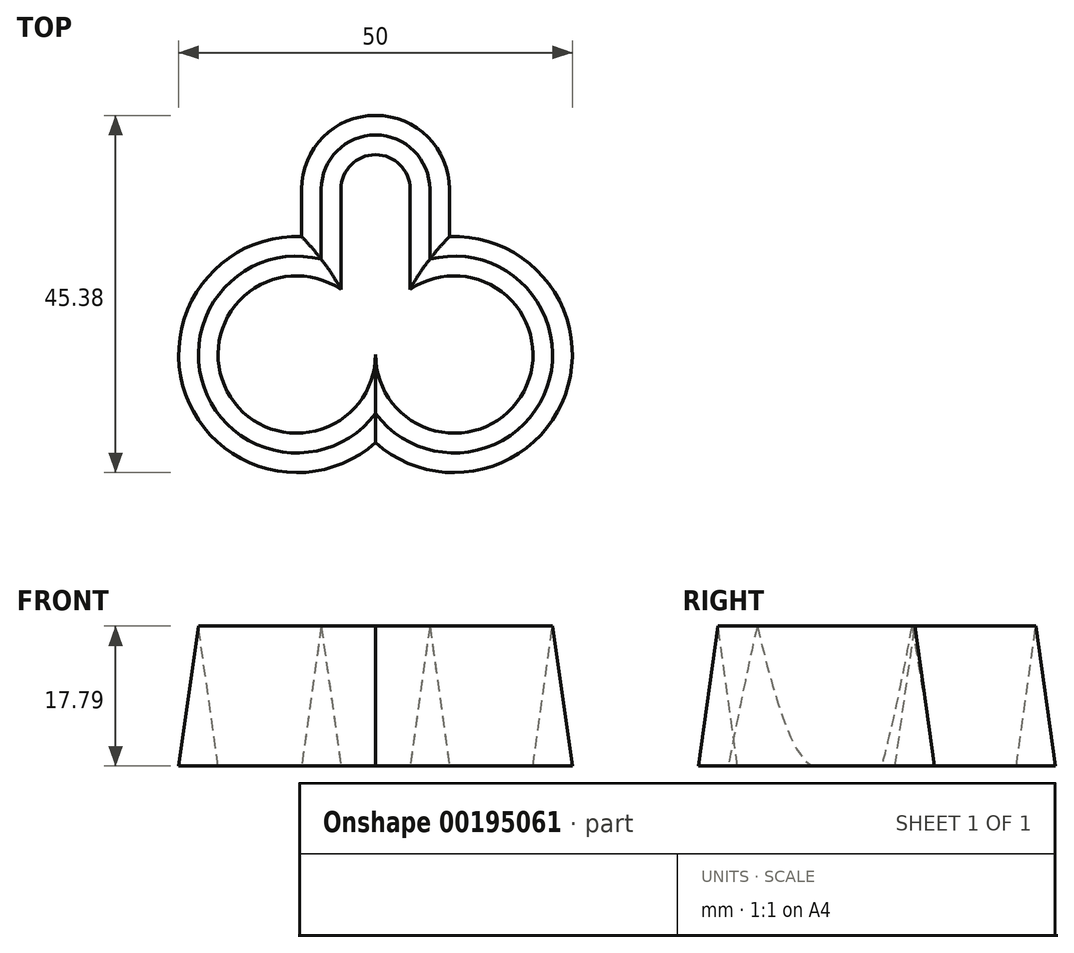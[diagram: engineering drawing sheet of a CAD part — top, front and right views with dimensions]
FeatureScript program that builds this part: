
annotation { "Feature Type Name" : "Feature", "Feature Type Description" : "" }
export const myFeature = defineFeature(function(context is Context, id is Id, definition is map)
    precondition{}
    {
        {
            var Q0;
            Q0=qCreatedBy(makeId("Top.planeOp"),FACE);
            var sketch = newSketch(context, id + "F0", { "sketchPlane" : qUnion([Q0])});
            skArc(sketch, "E0", {"start": v(4.4, 20.99) * mm, "mid": v(0, 25.38) * mm, "end": v(-4.4, 20.99) * mm});
            skArc(sketch, "E1", {"start": v(0, 0) * mm, "mid": v(18.83, -4.69) * mm, "end": v(4.4, 8.28) * mm});
            skArc(sketch, "E2", {"start": v(-4.4, 8.28) * mm, "mid": v(-18.83, -4.69) * mm, "end": v(0, 0) * mm});
            skLineSegment(sketch, "E3", {"start": v(-4.4, 20.99) * mm, "end": v(-4.4, 8.28) * mm});
            skLineSegment(sketch, "E4", {"start": v(4.4, 20.99) * mm, "end": v(4.4, 8.28) * mm});
            skArc(sketch, "E5.0", {"start": v(-9.4, 14.99) * mm, "mid": v(-24.12, -5.07) * mm, "end": v(0, -11.18) * mm});
            skLineSegment(sketch, "E5.1", {"start": v(-9.4, 20.99) * mm, "end": v(-9.4, 14.99) * mm});
            skArc(sketch, "E5.2", {"start": v(0, -11.18) * mm, "mid": v(24.12, -5.07) * mm, "end": v(9.4, 14.99) * mm});
            skLineSegment(sketch, "E5.3", {"start": v(9.4, 20.99) * mm, "end": v(9.4, 14.99) * mm});
            skArc(sketch, "E5.4", {"start": v(9.4, 20.99) * mm, "mid": v(0, 30.38) * mm, "end": v(-9.4, 20.99) * mm});
            skSolve(sketch);
        }
        {
            var Q0;
            Q0=makeQuery(id+"F0.imprint","IMPRINT",FACE,{"disambiguationData":[TD([[makeQuery(id+"F0.imprint","IMPRINT",EDGE,{"derivedFrom":sQuery(id+"F0.wireOp",EDGE,"E0")}),-1.0]])]});
            extrude(context, id + "F1", {"entities" : qUnion([Q0]), "depth" : 25 * mm, "hasDraft" : true, "draftAngle" : 8 * degree, "draftPullDirection" : true});
        }
    });
